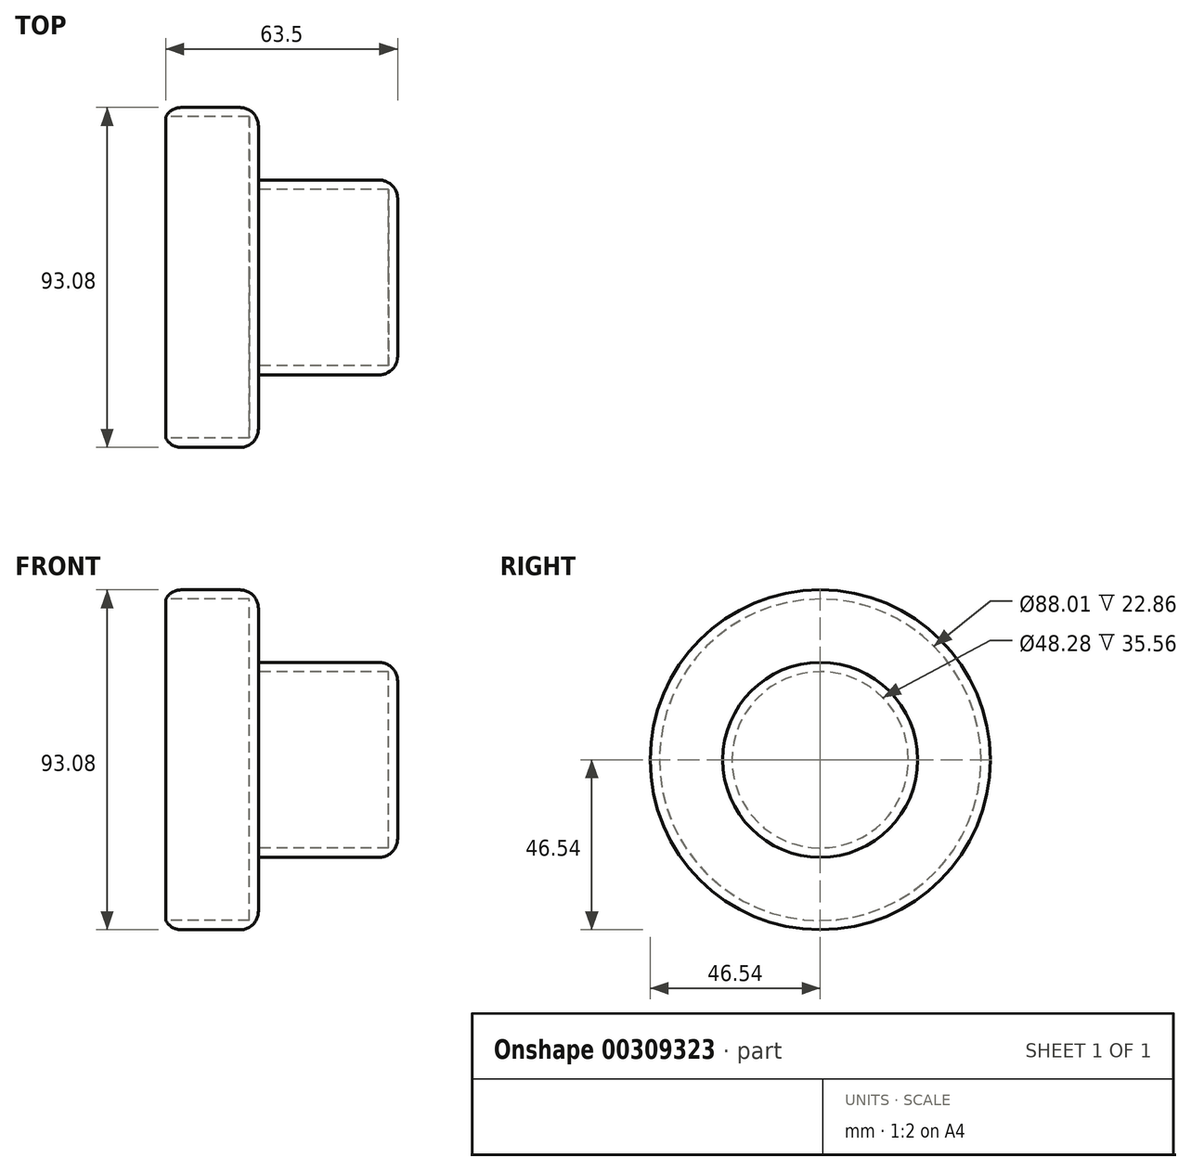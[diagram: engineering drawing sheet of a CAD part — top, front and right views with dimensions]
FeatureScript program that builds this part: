
annotation { "Feature Type Name" : "Feature", "Feature Type Description" : "" }
export const myFeature = defineFeature(function(context is Context, id is Id, definition is map)
    precondition{}
    {
        {
            var Q0;
            Q0=qCreatedBy(makeId("Right.planeOp"),FACE);
            var sketch = newSketch(context, id + "F0", { "sketchPlane" : qUnion([Q0])});
            skCircle(sketch, "E0", {"center": v(0, 0) * mm, "radius": 46.54 * mm});
            skSolve(sketch);
        }
        {
            var Q0;
            Q0=makeQuery(id+"F0.imprint","IMPRINT",FACE,{"disambiguationData":[TD([[makeQuery(id+"F0.imprint","IMPRINT",EDGE,{"derivedFrom":sQuery(id+"F0.wireOp",EDGE,"E0")}),1.0]])]});
            extrude(context, id + "F1", {"entities" : qUnion([Q0]), "depth" : 25.4 * mm});
        }
        {
            var Q0;
            Q0=makeQuery(id+"F1.opExtrude","CAP_FACE",FACE,{"disambiguationData":[OSD([sQuery(id+"F0.wireOp",EDGE,"E0")])],"isStart":true});
            shell(context, id + "F2", {"entities" : qUnion([Q0]), "thickness" : 2.54 * mm});
        }
        {
            var Q0;
            Q0=makeQuery(id+"F1.opExtrude","CAP_FACE",FACE,{"disambiguationData":[OSD([sQuery(id+"F0.wireOp",EDGE,"E0")])],"isStart":false});
            var sketch = newSketch(context, id + "F3", { "sketchPlane" : qUnion([Q0])});
            skCircle(sketch, "E1", {"center": v(0, 0) * mm, "radius": 26.68 * mm});
            skSolve(sketch);
        }
        {
            var Q0;
            Q0=makeQuery(id+"F3.imprint","IMPRINT",FACE,{"disambiguationData":[TD([[makeQuery(id+"F3.imprint","IMPRINT",EDGE,{"derivedFrom":sQuery(id+"F3.wireOp",EDGE,"E1")}),1.0]])]});
            extrude(context, id + "F4", {"entities" : qUnion([Q0]), "operationType" : NewBodyOperationType.ADD, "depth" : 38.1 * mm});
        }
        {
            var Q0;
            Q0=makeQuery(id+"F1.opExtrude","CAP_FACE",FACE,{"disambiguationData":[OSD([sQuery(id+"F0.wireOp",EDGE,"E0")])],"isStart":false});
            shell(context, id + "F5", {"entities" : qUnion([Q0]), "thickness" : 2.54 * mm});
        }
        {
            var Q0;
            Q0=makeQuery(id+"F1.opExtrude","CAP_EDGE",EDGE,{"disambiguationData":[OSD([sQuery(id+"F0.wireOp",EDGE,"E0")])],"isStart":true});
            var Q1;
            Q1=makeQuery(id+"F1.opExtrude","CAP_EDGE",EDGE,{"disambiguationData":[OSD([sQuery(id+"F0.wireOp",EDGE,"E0")])],"isStart":false});
            var Q2;
            Q2=makeQuery(id+"F4.opExtrude","CAP_EDGE",EDGE,{"disambiguationData":[OSD([sQuery(id+"F3.wireOp",EDGE,"E1")])],"isStart":false});
            fillet(context, id + "F6", {"entities" : qUnion([Q0, Q1, Q2]), "radius" : 5.08 * mm, "tangentPropagation" : true, "allowEdgeOverflow" : false});
        }
    });
